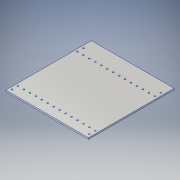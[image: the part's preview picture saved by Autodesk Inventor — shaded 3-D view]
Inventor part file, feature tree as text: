
AUTODESK INVENTOR PART (.ipt)
format: ipt  version: 2016 (Build 200138000, 138)  size: 162,304 bytes
history: native  units: in
note: dims shown in document units (in); Inventor stores cm internally (conversion verified against a paired STEP export)
features: reference x31, sketch x2, extrude x1, hole x1
ambient origin geometry x8: Origin, YZ Plane, XZ Plane, XY Plane, X Axis, Y Axis, Z Axis, Center Point
bodies: Solid1 (feature_tree)
feature tree (35):
  extrude  "Extrusion1"  Depth=8.7402in
  hole  "Hole1"  [1 undecoded]
  sketch  "Sketch1"  dims[d0=9.0551in d1=8.7402in]
  sketch  "Sketch2"  dims[d5=8.189in d6=7.5591in d7=0.1575in d8=0.1575in d9=0.1575in d10=0.1575in d11=0.1575in d12=0.0in d13=1.378in d14=0.6296in d15=0.1496in d16=0.75in d17=0.375in d18=0.25in d19=0.5635in d20=1.0in d21=0.8108in]
  reference  "Reference1"
  reference  "Reference2"
  reference  "Reference3"
  reference  "Reference4"
  reference  "Reference5"
  reference  "Reference6"
  reference  "Reference7"
  reference  "Reference8"
  reference  "Reference9"
  reference  "Reference10"
  reference  "Reference11"
  reference  "Reference12"
  reference  "Reference13"
  reference  "Reference14"
  reference  "Reference15"
  reference  "Reference16"
  reference  "Reference17"
  reference  "Reference18"
  reference  "Reference19"
  reference  "Reference20"
  reference  "Reference21"
  reference  "Reference22"
  reference  "Reference23"
  reference  "Reference24"
  reference  "Reference25"
  reference  "Reference26"
  reference  "Reference27"
  reference  "Reference28"
  reference  "Reference29"
  reference  "Reference30"
  reference  "Reference31"
note: 1 required parameter value undecoded (feature->parameter linkage not recoverable at this tier; creation-order binding heuristic only, values carry confidence <= 0.55)
